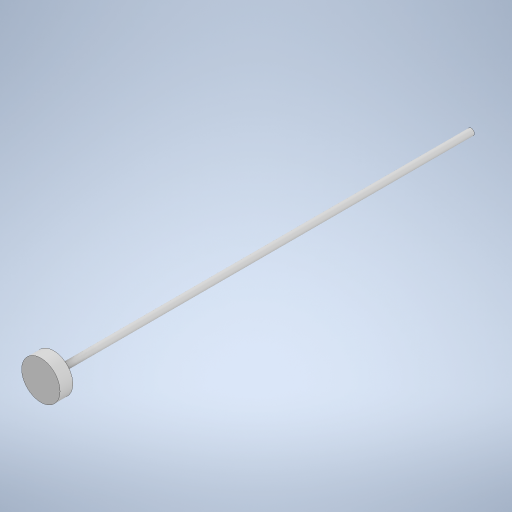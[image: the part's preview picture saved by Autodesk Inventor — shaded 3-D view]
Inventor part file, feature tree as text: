
AUTODESK INVENTOR PART (.ipt)
format: ipt  version: 2023.2 (Build 272271000, 271)  size: 241,664 bytes
history: native  units: mm
features: extrude x2, sketch x2
ambient origin geometry x8: Origin, YZ Plane, XZ Plane, XY Plane, X Axis, Y Axis, Z Axis, Center Point
bodies: Solid1 (feature_tree)
feature tree (4):
  extrude  "Extrusion1"  Depth=98.0mm TaperAngle=0.0deg
  extrude  "Extrusion2"  Depth=3.0mm TaperAngle=0.0deg
  sketch  "Sketch1"  dims[d0=1.5mm d1=98.0mm d2=0.0mm]
  sketch  "Sketch2"  dims[d3=9.0mm d4=3.0mm d5=0.0mm]
